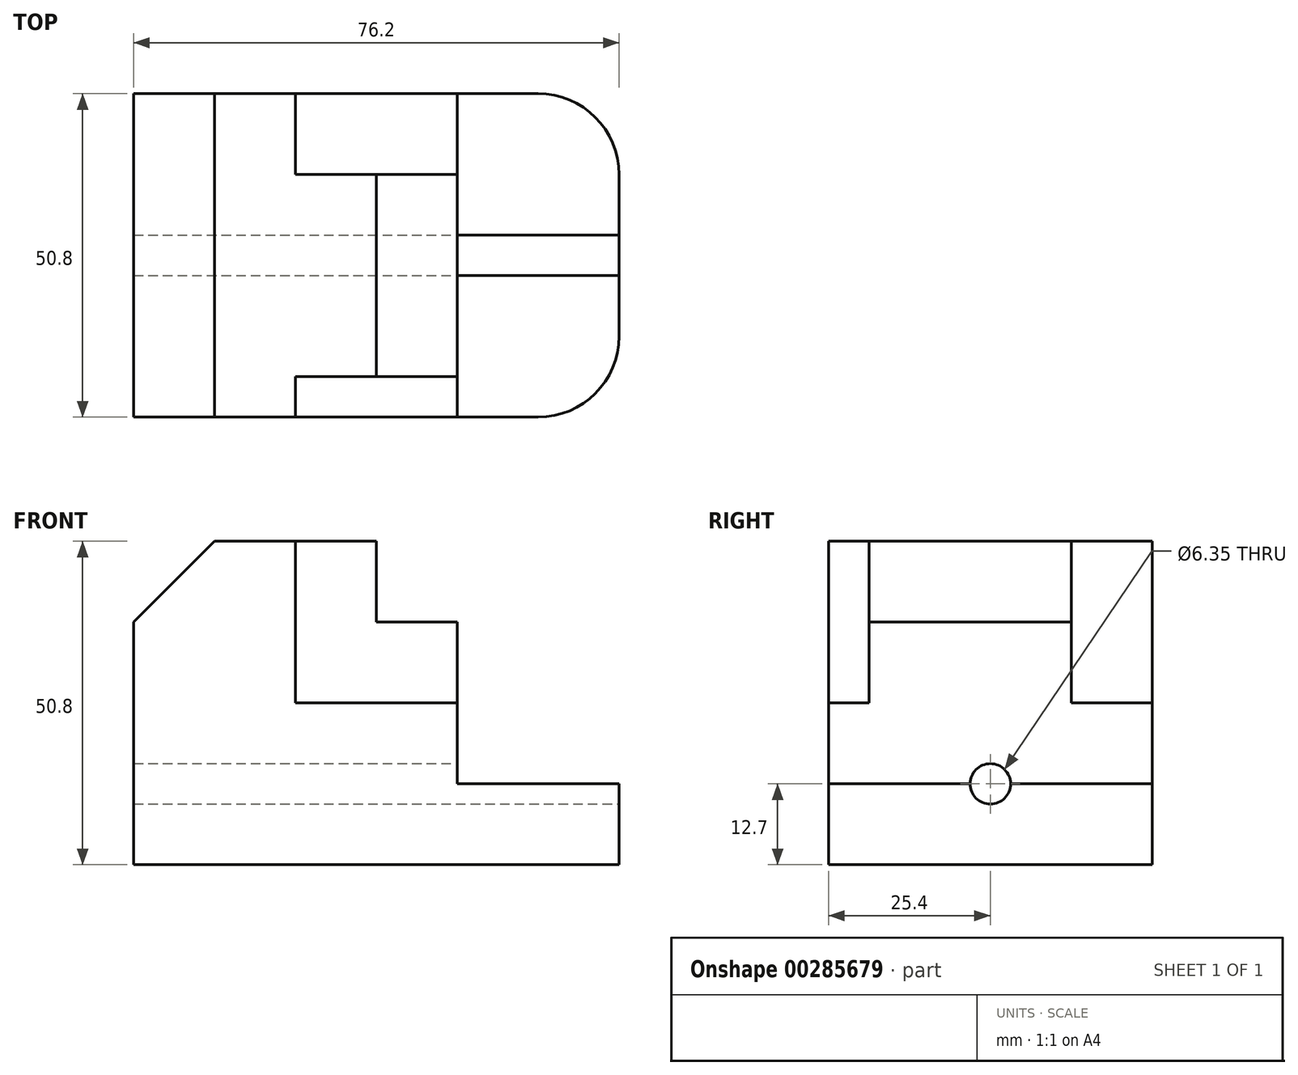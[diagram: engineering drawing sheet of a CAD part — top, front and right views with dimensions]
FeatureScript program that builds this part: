
annotation { "Feature Type Name" : "Feature", "Feature Type Description" : "" }
export const myFeature = defineFeature(function(context is Context, id is Id, definition is map)
    precondition{}
    {
        {
            var Q0;
            Q0=qCreatedBy(makeId("Front.planeOp"),FACE);
            var sketch = newSketch(context, id + "F0", { "sketchPlane" : qUnion([Q0])});
            skLineSegment(sketch, "E0", {"start": v(0, 0) * mm, "end": v(0, 38.1) * mm});
            skLineSegment(sketch, "E1", {"start": v(0, 38.1) * mm, "end": v(12.7, 50.8) * mm});
            skLineSegment(sketch, "E2", {"start": v(12.7, 50.8) * mm, "end": v(38.1, 50.8) * mm});
            skLineSegment(sketch, "E3", {"start": v(38.1, 50.8) * mm, "end": v(38.1, 38.1) * mm});
            skLineSegment(sketch, "E4", {"start": v(38.1, 38.1) * mm, "end": v(50.8, 38.1) * mm});
            skLineSegment(sketch, "E5", {"start": v(50.8, 38.1) * mm, "end": v(50.8, 12.7) * mm});
            skLineSegment(sketch, "E6", {"start": v(50.8, 12.7) * mm, "end": v(76.2, 12.7) * mm});
            skLineSegment(sketch, "E7", {"start": v(76.2, 12.7) * mm, "end": v(76.2, 0) * mm});
            skLineSegment(sketch, "E8", {"start": v(76.2, 0) * mm, "end": v(0, 0) * mm});
            skSolve(sketch);
        }
        {
            var Q0;
            Q0=makeQuery(id+"F0.imprint","IMPRINT",FACE,{"disambiguationData":[TD([[makeQuery(id+"F0.imprint","IMPRINT",EDGE,{"derivedFrom":sQuery(id+"F0.wireOp",EDGE,"E0")}),-1.0]])]});
            extrude(context, id + "F1", {"entities" : qUnion([Q0]), "depth" : 50.8 * mm});
        }
        {
            var Q0;
            Q0=makeQuery(id+"F1.opExtrude","CAP_FACE",FACE,{"disambiguationData":[OSD([sQuery(id+"F0.wireOp",EDGE,"E0"),sQuery(id+"F0.wireOp",EDGE,"E1"),sQuery(id+"F0.wireOp",EDGE,"E2"),sQuery(id+"F0.wireOp",EDGE,"E3"),sQuery(id+"F0.wireOp",EDGE,"E4"),sQuery(id+"F0.wireOp",EDGE,"E5"),sQuery(id+"F0.wireOp",EDGE,"E6"),sQuery(id+"F0.wireOp",EDGE,"E7"),sQuery(id+"F0.wireOp",EDGE,"E8")])],"isStart":false});
            var sketch = newSketch(context, id + "F2", { "sketchPlane" : qUnion([Q0])});
            skLineSegment(sketch, "E9", {"start": v(25.4, 50.8) * mm, "end": v(25.4, 25.4) * mm});
            skLineSegment(sketch, "E10", {"start": v(25.4, 25.4) * mm, "end": v(50.8, 25.4) * mm});
            skLineSegment(sketch, "E11", {"start": v(50.8, 25.4) * mm, "end": v(50.8, 38.1) * mm});
            skLineSegment(sketch, "E12", {"start": v(50.8, 38.1) * mm, "end": v(38.1, 38.1) * mm});
            skLineSegment(sketch, "E13", {"start": v(38.1, 38.1) * mm, "end": v(38.1, 50.8) * mm});
            skLineSegment(sketch, "E14", {"start": v(38.1, 50.8) * mm, "end": v(25.4, 50.8) * mm});
            skSolve(sketch);
        }
        {
            var Q0;
            Q0=makeQuery(id+"F2.imprint","IMPRINT",FACE,{"disambiguationData":[TD([[makeQuery(id+"F2.imprint","IMPRINT",EDGE,{"derivedFrom":sQuery(id+"F2.wireOp",EDGE,"E9")}),1.0]])]});
            extrude(context, id + "F3", {"entities" : qUnion([Q0]), "operationType" : NewBodyOperationType.REMOVE, "endBound" : BoundingType.SYMMETRIC, "oppositeDirection" : true, "depth" : 12.7 * mm});
        }
        {
            var Q0;
            Q0=makeQuery(id+"F1.opExtrude","CAP_FACE",FACE,{"disambiguationData":[OSD([sQuery(id+"F0.wireOp",EDGE,"E0"),sQuery(id+"F0.wireOp",EDGE,"E1"),sQuery(id+"F0.wireOp",EDGE,"E2"),sQuery(id+"F0.wireOp",EDGE,"E3"),sQuery(id+"F0.wireOp",EDGE,"E4"),sQuery(id+"F0.wireOp",EDGE,"E5"),sQuery(id+"F0.wireOp",EDGE,"E6"),sQuery(id+"F0.wireOp",EDGE,"E7"),sQuery(id+"F0.wireOp",EDGE,"E8")])],"isStart":true});
            var sketch = newSketch(context, id + "F4", { "sketchPlane" : qUnion([Q0])});
            skLineSegment(sketch, "E15", {"start": v(-25.4, 50.8) * mm, "end": v(-25.4, 25.4) * mm});
            skLineSegment(sketch, "E16", {"start": v(-25.4, 25.4) * mm, "end": v(-50.8, 25.4) * mm});
            skLineSegment(sketch, "E17", {"start": v(-50.8, 25.4) * mm, "end": v(-50.8, 38.1) * mm});
            skLineSegment(sketch, "E18", {"start": v(-50.8, 38.1) * mm, "end": v(-38.1, 38.1) * mm});
            skLineSegment(sketch, "E19", {"start": v(-38.1, 38.1) * mm, "end": v(-38.1, 50.8) * mm});
            skLineSegment(sketch, "E20", {"start": v(-38.1, 50.8) * mm, "end": v(-25.4, 50.8) * mm});
            skSolve(sketch);
        }
        {
            var Q0;
            Q0=makeQuery(id+"F4.imprint","IMPRINT",FACE,{"disambiguationData":[TD([[makeQuery(id+"F4.imprint","IMPRINT",EDGE,{"derivedFrom":sQuery(id+"F4.wireOp",EDGE,"E15")}),-1.0]])]});
            extrude(context, id + "F5", {"entities" : qUnion([Q0]), "operationType" : NewBodyOperationType.REMOVE, "oppositeDirection" : true, "depth" : 12.7 * mm});
        }
        {
            var Q0;
            Q0=makeQuery(id+"F1.opExtrude","SWEPT_FACE",FACE,{"disambiguationData":[OSD([sQuery(id+"F0.wireOp",EDGE,"E7")])]});
            var sketch = newSketch(context, id + "F6", { "sketchPlane" : qUnion([Q0])});
            skCircle(sketch, "E21", {"center": v(-25.4, 12.7) * mm, "radius": 3.18 * mm});
            skSolve(sketch);
        }
        {
            var Q0;
            {var subQ0=sQuery(id+"F6.wireOp",EDGE,"E21");var subQ1=makeQuery(id+"F1.opExtrude","SWEPT_EDGE",EDGE,{"disambiguationData":[OSD([sQuery(id+"F0.wireOp",EDGE,"E6"),sQuery(id+"F0.wireOp",EDGE,"E7")])]});var subQ2=makeQuery(id+"F6.imprint","INTERSECT",VERTEX,{"disambiguationData":[OD(0.0)],"derivedFrom":[subQ1,subQ0]});Q0=makeQuery(id+"F6.imprint","IMPRINT",FACE,{"disambiguationData":[TD([[makeQuery(id+"F6.imprint","IMPRINT",EDGE,{"disambiguationData":[TD([[subQ2,1.0]])],"derivedFrom":subQ0}),1.0]])]});}
            var Q1;
            {var subQ0=sQuery(id+"F6.wireOp",EDGE,"E21");var subQ1=makeQuery(id+"F1.opExtrude","SWEPT_EDGE",EDGE,{"disambiguationData":[OSD([sQuery(id+"F0.wireOp",EDGE,"E6"),sQuery(id+"F0.wireOp",EDGE,"E7")])]});var subQ2=makeQuery(id+"F6.imprint","INTERSECT",VERTEX,{"disambiguationData":[OD(0.0)],"derivedFrom":[subQ1,subQ0]});Q1=makeQuery(id+"F6.imprint","IMPRINT",FACE,{"disambiguationData":[TD([[makeQuery(id+"F6.imprint","IMPRINT",EDGE,{"disambiguationData":[TD([[subQ2,-1.0]])],"derivedFrom":subQ0}),1.0]])]});}
            extrude(context, id + "F7", {"entities" : qUnion([Q0, Q1]), "operationType" : NewBodyOperationType.REMOVE, "oppositeDirection" : true, "depth" : 76.2 * mm});
        }
        {
            var Q0;
            Q0=makeQuery(id+"F1.opExtrude","CAP_EDGE",EDGE,{"disambiguationData":[OSD([sQuery(id+"F0.wireOp",EDGE,"E7")])],"isStart":false});
            var Q1;
            Q1=makeQuery(id+"F1.opExtrude","CAP_EDGE",EDGE,{"disambiguationData":[OSD([sQuery(id+"F0.wireOp",EDGE,"E7")])],"isStart":true});
            fillet(context, id + "F8", {"entities" : qUnion([Q0, Q1]), "radius" : 12.7 * mm, "tangentPropagation" : true, "allowEdgeOverflow" : false});
        }
    });
